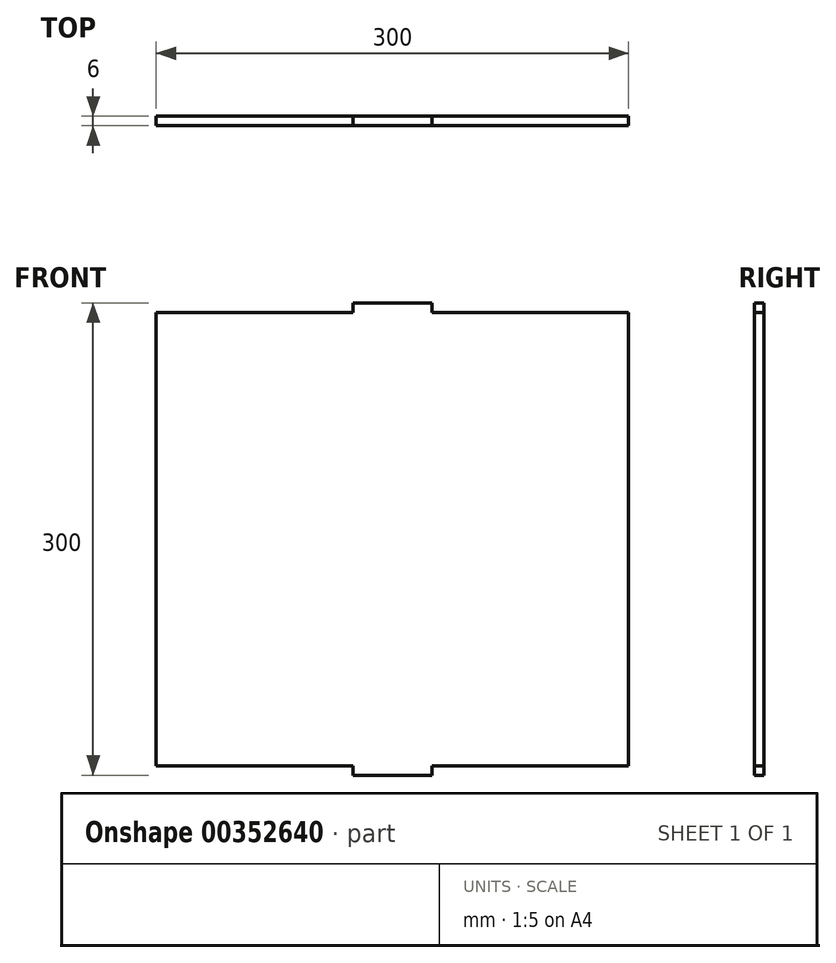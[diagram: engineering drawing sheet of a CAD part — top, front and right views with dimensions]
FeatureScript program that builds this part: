
annotation { "Feature Type Name" : "Feature", "Feature Type Description" : "" }
export const myFeature = defineFeature(function(context is Context, id is Id, definition is map)
    precondition{}
    {
        {
            var Q0;
            Q0=qCreatedBy(makeId("Front.planeOp"),FACE);
            var sketch = newSketch(context, id + "F0", { "sketchPlane" : qUnion([Q0])});
            skLineSegment(sketch, "E0.left", {"start": v(-180.97, 208.5) * mm, "end": v(-180.97, -79.5) * mm});
            skLineSegment(sketch, "E1", {"start": v(-180.97, -79.5) * mm, "end": v(-55.97, -79.5) * mm});
            skLineSegment(sketch, "E2", {"start": v(119.03, -79.5) * mm, "end": v(119.03, 208.5) * mm});
            skLineSegment(sketch, "E3", {"start": v(-55.97, 214.5) * mm, "end": v(-55.97, 208.5) * mm});
            skLineSegment(sketch, "E4", {"start": v(-5.97, 208.5) * mm, "end": v(-5.97, 214.5) * mm});
            skLineSegment(sketch, "E5", {"start": v(-55.97, 214.5) * mm, "end": v(-5.97, 214.5) * mm});
            skLineSegment(sketch, "E6", {"start": v(-55.97, 208.5) * mm, "end": v(-180.97, 208.5) * mm});
            skLineSegment(sketch, "E7", {"start": v(-5.97, 208.5) * mm, "end": v(119.03, 208.5) * mm});
            skLineSegment(sketch, "E8", {"start": v(-55.97, -79.5) * mm, "end": v(-55.97, -85.5) * mm});
            skLineSegment(sketch, "E9", {"start": v(-55.97, -85.5) * mm, "end": v(-5.97, -85.5) * mm});
            skLineSegment(sketch, "E10", {"start": v(-5.97, -85.5) * mm, "end": v(-5.97, -79.5) * mm});
            skLineSegment(sketch, "E11.trimOffspring", {"start": v(-5.97, -79.5) * mm, "end": v(119.03, -79.5) * mm});
            skSolve(sketch);
        }
        {
            var Q0;
            Q0=qSketchRegion(id+"F0",true);
            extrude(context, id + "F1", {"entities" : qUnion([Q0]), "depth" : 6 * mm});
        }
    });
